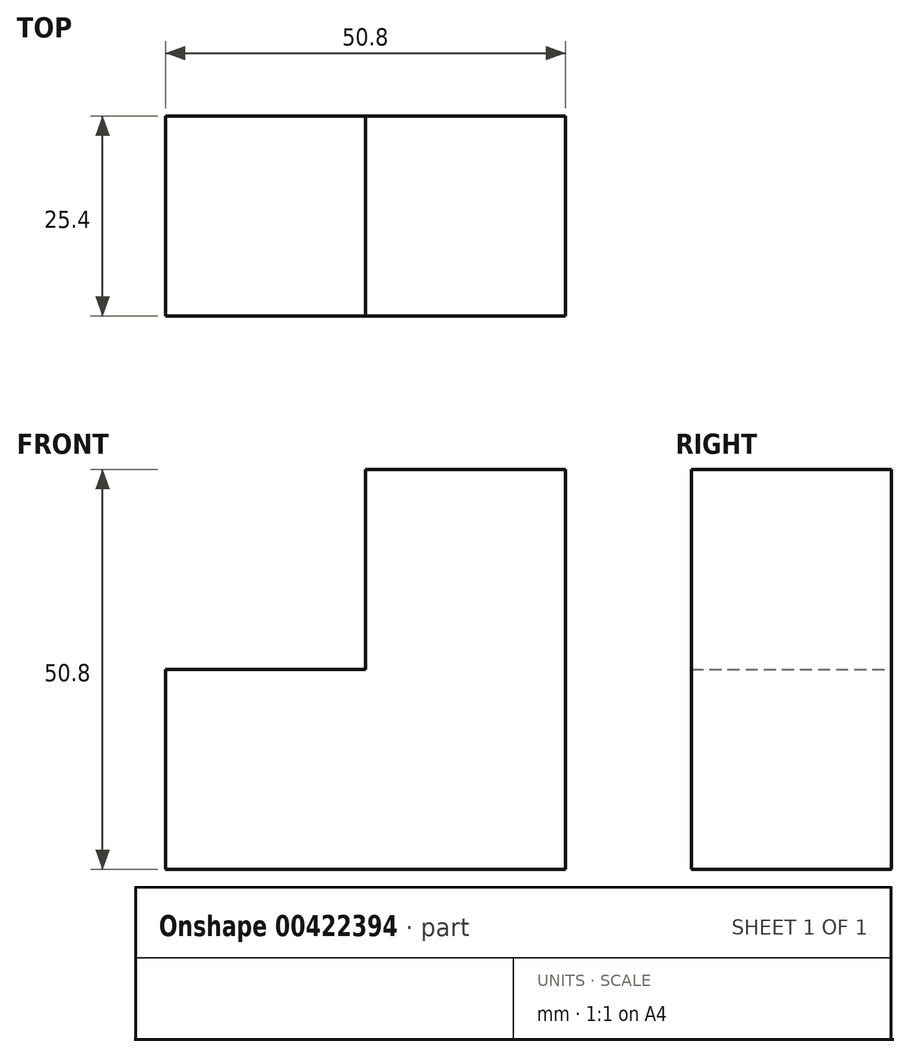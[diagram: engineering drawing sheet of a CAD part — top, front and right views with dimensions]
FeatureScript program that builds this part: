
annotation { "Feature Type Name" : "Feature", "Feature Type Description" : "" }
export const myFeature = defineFeature(function(context is Context, id is Id, definition is map)
    precondition{}
    {
        {
            var Q0;
            Q0=qCreatedBy(makeId("Front.planeOp"),FACE);
            var sketch = newSketch(context, id + "F0", { "sketchPlane" : qUnion([Q0])});
            skLineSegment(sketch, "E0", {"start": v(0, 0) * mm, "end": v(0, 50.8) * mm});
            skLineSegment(sketch, "E1", {"start": v(0, 50.8) * mm, "end": v(-25.4, 50.8) * mm});
            skLineSegment(sketch, "E2", {"start": v(-25.4, 50.8) * mm, "end": v(-25.4, 25.4) * mm});
            skLineSegment(sketch, "E3", {"start": v(-25.4, 25.4) * mm, "end": v(-50.8, 25.4) * mm});
            skLineSegment(sketch, "E4", {"start": v(-50.8, 25.4) * mm, "end": v(-50.8, 0) * mm});
            skLineSegment(sketch, "E5", {"start": v(-50.8, 0) * mm, "end": v(0, 0) * mm});
            skSolve(sketch);
        }
        {
            var Q0;
            Q0 = qSketchRegion(id + "F0", true);
            extrude(context, id + "F1", {"entities" : qUnion([Q0]), "depth" : 25.4 * mm});
        }
    });
